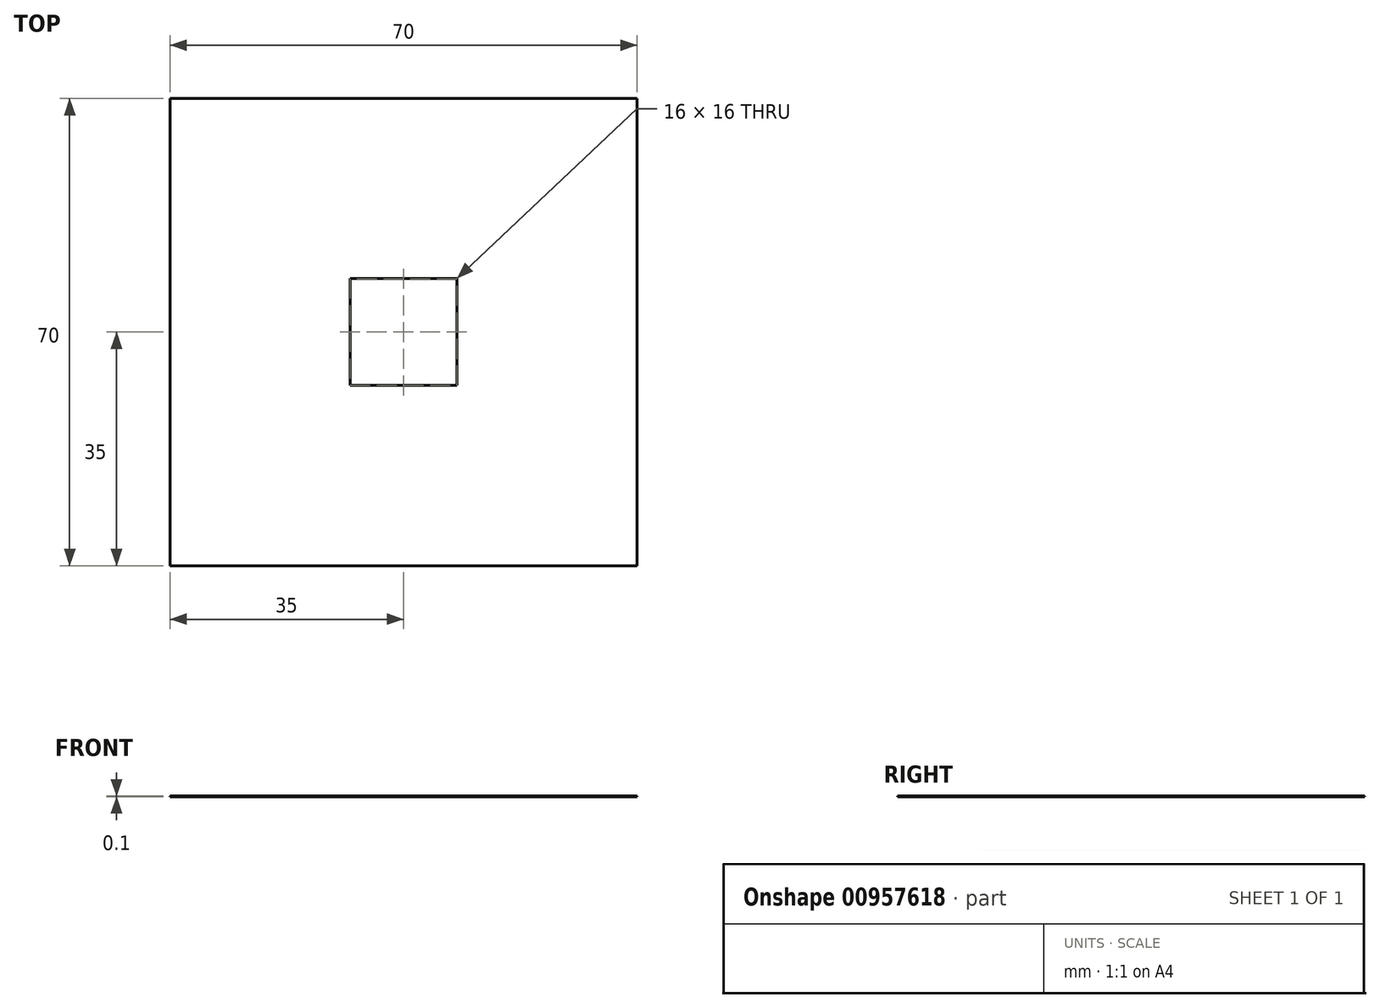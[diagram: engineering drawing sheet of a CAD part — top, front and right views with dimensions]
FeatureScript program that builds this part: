
annotation { "Feature Type Name" : "Feature", "Feature Type Description" : "" }
export const myFeature = defineFeature(function(context is Context, id is Id, definition is map)
    precondition{}
    {
        {
            var Q0;
            Q0=qCreatedBy(makeId("Top.planeOp"),FACE);
            var sketch = newSketch(context, id + "F0", { "sketchPlane" : qUnion([Q0])});
            skLineSegment(sketch, "E0.bottom", {"start": v(35, 35) * mm, "end": v(-35, 35) * mm});
            skLineSegment(sketch, "E0.top", {"start": v(35, -35) * mm, "end": v(-35, -35) * mm});
            skLineSegment(sketch, "E0.left", {"start": v(35, 35) * mm, "end": v(35, -35) * mm});
            skLineSegment(sketch, "E0.right", {"start": v(-35, 35) * mm, "end": v(-35, -35) * mm});
            skPoint(sketch, "E0.middle", {"position": v(0, 0) * mm});
            skLineSegment(sketch, "E1.bottom", {"start": v(8, 8) * mm, "end": v(-8, 8) * mm});
            skLineSegment(sketch, "E1.top", {"start": v(8, -8) * mm, "end": v(-8, -8) * mm});
            skLineSegment(sketch, "E1.left", {"start": v(8, 8) * mm, "end": v(8, -8) * mm});
            skLineSegment(sketch, "E1.right", {"start": v(-8, 8) * mm, "end": v(-8, -8) * mm});
            skSolve(sketch);
        }
        {
            var Q0;
            Q0=makeQuery(id+"F0.imprint","IMPRINT",FACE,{"disambiguationData":[TD([[makeQuery(id+"F0.imprint","IMPRINT",EDGE,{"derivedFrom":sQuery(id+"F0.wireOp",EDGE,"E0.bottom")}),1.0]])]});
            extrude(context, id + "F1", {"entities" : qUnion([Q0]), "depth" : 0.1 * mm, "offsetDistance" : 25 * mm});
        }
    });
